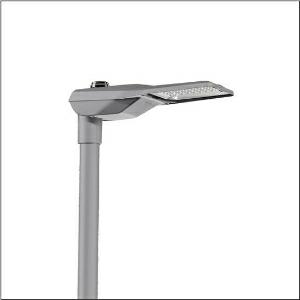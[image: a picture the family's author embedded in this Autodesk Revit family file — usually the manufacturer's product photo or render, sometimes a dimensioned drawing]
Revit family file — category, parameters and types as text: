
# Revit family: streetlight_sl_21_mini___st0_8a_5xe6c37n08gb_efcc
name_source: partatom
category: Lighting Fixtures
units: mm (PartAtom-declared; Revit-internal decimal feet)

## family parameters
Cut with Voids When Loaded = No
Host = Face
Light Source = No
Part Type = Normal
Room Calculation Point = No
Round Connector Dimension = Use Diameter
Shared = No

## types (1)
- --- (1 x LED, 5940 lm, 40.4 W, 3000K)
    Apparent Load = 40 VA
    CIE Flux Codes = 38 75 97 100 100
    Color Rendering = 70
    Color Temperature = 3000K
    Default Elevation = 1800 mm
    Description = Streetlight SL 21 mini, mast luminaire, primary light control with lens, of PMMA, primary optical cover: cover, of toughened safety glass, transparent, light distribution: ST0.8a, light emission: direct distribution, primary light characteristic: asymmetric, installation type: side-entry, LED, 3G 1.5mm², High Power LED, rated luminous flux: 5.940lm, luminous efficacy: 147lm/W, light colour: 730, colour temperature: 3000K, control gear: NEMA (7pin), control: overheat protection, pre-setting: linear dimming characteristic, constant luminous flux control, time-dependent luminous flux control, flexible luminous flux parameterisation, mains connection: 230..240V, AC, 50/60Hz, connection cable pre-assembled, cable length: 8,5m, wiring characteristics: H07RN-F, start of lifetime: 40W, end of service life: 41W, reduction: 19W, luminaire housing, of diecast aluminium (EN AC-44300), powder-coated, SITECO metallic grey (DB 702S), corrosivity category C5 high according to DIN EN ISO 12944, multi-level sealing system, sealing non-destructively replaceable, inclination adjustable: 0°, 5°, 10°, 15°, length: 628mm, width: 235mm, height: 110mm, spigot size: 42mm (side-entry), mounting height: 4..8m, protection rating (complete): IP66, insulation class (complete): insulation class I (protective earthing), certification: CE, ENEC, ENEC+, VDE, impact resistance: IK10, permissible operating ambient temperature for outdoor applications: -40..+50°C, standard-compliant lighting for roads and squares, packaging unit: 1 piece

Light Distribution: ST0.8a
    Height = 110 mm
    Lamp = 1 x LED
    Lamp Light Flux = 5940 lm
    Lamp Power = 40.4 W
    Lamp count = 1
    Length = 625 mm
    Luminous efficacy = 147 lm/W
    Manufacturer = Siteco
    ModVariant = No
    Model = 5XE6C37N08GB
    Number of Poles = 1
    OnlyDefault = Yes
    Power Factor = 1
    Product Name = Streetlight SL 21 mini | ST0.8a
    Product group = mast luminaire | pylon top
    ProductGroupID = 6100
    Protection Class = Protection class I
    Protection Degree = IP 66
    RLX_Detail_Level = 1
    RLX_Emergency_Light_Flux = 0 lm
    RLX_Emergency_Type = 0
    RLX_Emergency_Type_DB = No
    RlxData = <blob elided: 25897 chars, md5=d4841489>
    Socket = socket
    Standby Power = 0 W
    System Light Flux = 5940 lm
    System Power = 40 W
    Type Comments = factory setting: luminous flux: 100 % | dim-lin: 254 | 812 mA
    Type Image = l_1294379.jpg
    URL = http://relux.com
    VarID = @adj_133761
    Voltage = 0 V
    Weight = 0.00 kg
    Width = 234 mm

## geometry (parser evidence)
native form markers: Blend x4, Sweep x9
no freeform markers — native parametric forms only
